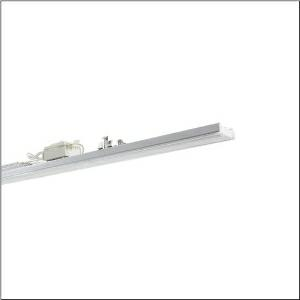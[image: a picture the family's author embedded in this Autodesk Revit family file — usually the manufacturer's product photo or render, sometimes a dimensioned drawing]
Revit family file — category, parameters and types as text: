
# Revit family: licross_21_recessed_ho_52te12dv4l2m3c
name_source: partatom
category: Lighting Fixtures
units: mm (PartAtom-declared; Revit-internal decimal feet)

## family parameters
Cut with Voids When Loaded = No
Host = Face
Light Source = No
Part Type = Normal
Room Calculation Point = No
Round Connector Dimension = Use Diameter
Shared = No

## types (1)
- --- (1 x LED, 910 lm, 6.4 W, 4000K)
    Apparent Load = 6 VA
    CIE Flux Codes = 69 91 98 100 100
    Color Rendering = 80
    Color Temperature = 4000K
    Default Elevation = 1800 mm
    Description = Licross 21 Recessed HO, luminaire insert, of sheet steel, galvanised, coil coated, white, length: 2.250mm, width: 66mm, height: 67mm, LED rated luminous flux: 22.710lm, light colour: 840, SDCM (Standard Deviation of Colour Matching)MacAdam ≤ 3 SDCM (initial), control gear: DALI 2 (for two DALI lines), with plug, 6-pole, with phase selection, for trunking rail, 14-core, mains connection: 220..240V, AC, 50/60Hz, rated input power: 129W, for trunking rail, 14-core, internal wiring halogen-free, for emergency light function, converter,control gear: single battery element, battery: LiFePO4, 9Ah, primary optical cover: cover, of PMMA, light emission: direct distribution, primary light characteristic: symmetric, protection rating (complete): IP54, insulation class (complete): insulation class I (protective earthing), certification: CE, UKCA, protection symbol: D if used in an environment with non-conductive dust loads with corresponding accessories, impact resistance: IK06, permissible ambient temperature for indoor applications: +5..+30°C, standard: EN 60598-2-22, LABS conformity tested according to VDMA 24364:2018-05, reducing of maximum allowable ambient temperature of 5°C with ceiling mounting, corresponds to IFS (International Featured Standards) requirements for safety and quality in the food industry, The light source and the operating device comply with the requirements of the Ecodesign Regulation (EU) 2019/2020 and are replaceable in accordance with this regulation, packaging unit: 1 piece
    Height = 58 mm
    Lamp = 1 x LED
    Lamp Light Flux = 910 lm
    Lamp Power = 6.4 W
    Lamp count = 1
    Length = 2250 mm
    Luminous efficacy = 142 lm/W
    Manufacturer = Siteco
    ModVariant = No
    Model = 52TE12DV4L2M3C
    Mounting Place = Ceiling
    Mounting Type = Pendant
    Number of Poles = 1
    OnlyDefault = Yes
    Power Factor = 1
    Product Name = Licross 21 Recessed HO
    Product group = luminaire insert | ceiling pendant
    ProductGroupID = 901
    Protection Class = Protection class I
    Protection Degree = IP 54
    RLX_Detail_Level = 1
    RLX_Emergency_Light_Flux = 0 lm
    RLX_Emergency_Type = 0
    RLX_Emergency_Type_DB = No
    RlxData = <blob elided: 30409 chars, md5=2fb5f191>
    Socket = socket
    Standby Power = 0 W
    System Light Flux = 910 lm
    System Power = 6 W
    Type Comments = : emergency light operation: 3 h
    Type Image = l_1296930.jpg
    URL = http://relux.com
    VarID = @adj_109233
    Voltage = 0 V
    Weight = 0.00 kg
    Width = 66 mm

## geometry (parser evidence)
native form markers: Blend x4, Sweep x10
no freeform markers — native parametric forms only
